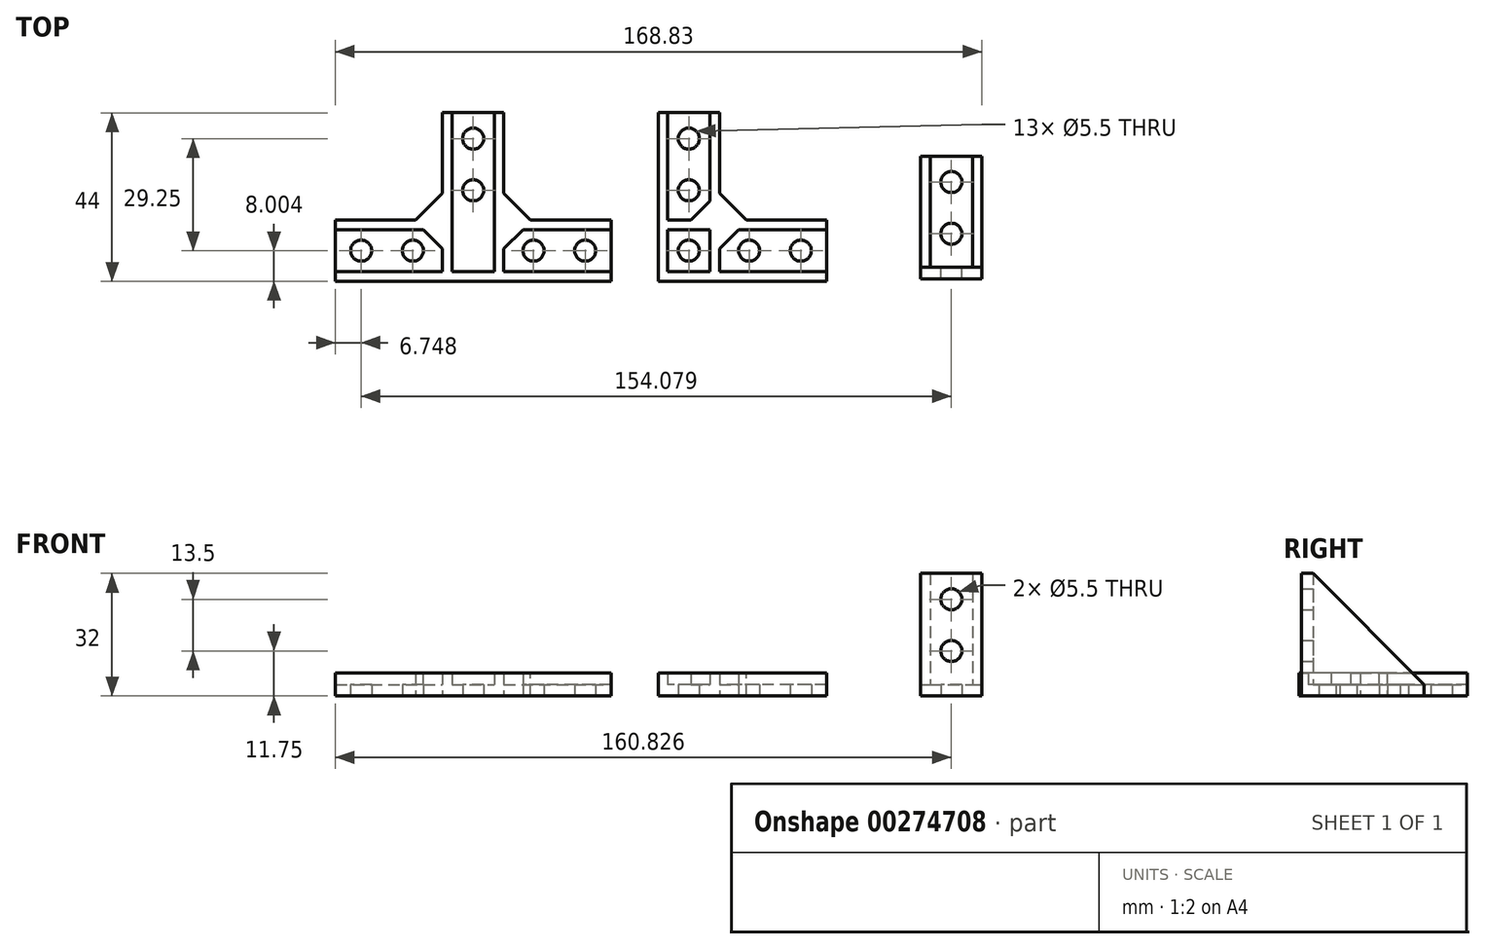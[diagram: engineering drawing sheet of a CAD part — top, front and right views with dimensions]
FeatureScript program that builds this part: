
annotation { "Feature Type Name" : "Feature", "Feature Type Description" : "" }
export const myFeature = defineFeature(function(context is Context, id is Id, definition is map)
    precondition{}
    {
        {
            var Q0;
            Q0=qCreatedBy(makeId("Top.planeOp"),FACE);
            var sketch = newSketch(context, id + "F0", { "sketchPlane" : qUnion([Q0])});
            skLineSegment(sketch, "E0", {"start": v(-54.8, -45.23) * mm, "end": v(-10.8, -45.23) * mm});
            skLineSegment(sketch, "E1", {"start": v(-10.8, -45.23) * mm, "end": v(-10.8, -29.23) * mm});
            skLineSegment(sketch, "E2", {"start": v(-10.8, -29.23) * mm, "end": v(-38.8, -29.23) * mm});
            skLineSegment(sketch, "E3", {"start": v(-38.8, -29.23) * mm, "end": v(-38.8, -1.23) * mm});
            skLineSegment(sketch, "E4", {"start": v(-38.8, -1.23) * mm, "end": v(-54.8, -1.23) * mm});
            skLineSegment(sketch, "E5", {"start": v(-54.8, -1.23) * mm, "end": v(-54.8, -45.23) * mm});
            skCircle(sketch, "E6", {"center": v(-17.54, -37.23) * mm, "radius": 2.75 * mm});
            skPoint(sketch, "E6.centerSnap0", {"position": v(-10.8, -37.23) * mm});
            skCircle(sketch, "E7", {"center": v(-31.04, -37.23) * mm, "radius": 2.75 * mm});
            skLineSegment(sketch, "E8", {"start": v(-54.8, -45.23) * mm, "end": v(-38.8, -29.23) * mm, "construction": true});
            skCircle(sketch, "E9.MirrorC", {"center": v(-46.8, -21.48) * mm, "radius": 2.75 * mm});
            skCircle(sketch, "E10.MirrorC", {"center": v(-46.8, -7.98) * mm, "radius": 2.75 * mm});
            skCircle(sketch, "E11", {"center": v(-46.8, -37.23) * mm, "radius": 2.75 * mm});
            skLineSegment(sketch, "E12", {"start": v(-67.07, -45.23) * mm, "end": v(-139.07, -45.23) * mm});
            skLineSegment(sketch, "E13", {"start": v(-139.07, -45.23) * mm, "end": v(-139.07, -29.23) * mm});
            skLineSegment(sketch, "E14", {"start": v(-139.07, -29.23) * mm, "end": v(-111.07, -29.23) * mm});
            skLineSegment(sketch, "E15", {"start": v(-111.07, -29.23) * mm, "end": v(-111.07, -1.23) * mm});
            skLineSegment(sketch, "E16", {"start": v(-111.07, -1.23) * mm, "end": v(-95.07, -1.23) * mm});
            skLineSegment(sketch, "E17", {"start": v(-95.07, -1.23) * mm, "end": v(-95.07, -29.23) * mm});
            skLineSegment(sketch, "E18", {"start": v(-95.07, -29.23) * mm, "end": v(-67.07, -29.23) * mm});
            skLineSegment(sketch, "E19", {"start": v(-67.07, -29.23) * mm, "end": v(-67.07, -45.23) * mm});
            skCircle(sketch, "E20", {"center": v(-73.82, -37.23) * mm, "radius": 2.75 * mm});
            skPoint(sketch, "E20.centerSnap0", {"position": v(-67.07, -37.23) * mm});
            skCircle(sketch, "E21", {"center": v(-87.32, -37.23) * mm, "radius": 2.75 * mm});
            skCircle(sketch, "E22", {"center": v(-103.07, -7.98) * mm, "radius": 2.75 * mm});
            skPoint(sketch, "E22.centerSnap0", {"position": v(-103.07, -1.23) * mm});
            skCircle(sketch, "E23", {"center": v(-103.07, -21.48) * mm, "radius": 2.75 * mm});
            skLineSegment(sketch, "E24", {"start": v(-103.07, -1.23) * mm, "end": v(-103.07, -45.23) * mm, "construction": true});
            skCircle(sketch, "E25.MirrorC", {"center": v(-118.82, -37.23) * mm, "radius": 2.75 * mm});
            skCircle(sketch, "E26.MirrorC", {"center": v(-132.32, -37.23) * mm, "radius": 2.75 * mm});
            skLineSegment(sketch, "E27", {"start": v(13.76, -44.56) * mm, "end": v(13.76, -12.56) * mm});
            skLineSegment(sketch, "E28", {"start": v(13.76, -12.56) * mm, "end": v(29.76, -12.56) * mm});
            skLineSegment(sketch, "E29", {"start": v(29.76, -12.56) * mm, "end": v(29.76, -44.56) * mm});
            skLineSegment(sketch, "E30", {"start": v(29.76, -44.56) * mm, "end": v(13.76, -44.56) * mm});
            skLineSegment(sketch, "E31", {"start": v(21.76, -12.56) * mm, "end": v(21.76, -44.56) * mm, "construction": true});
            skCircle(sketch, "E32", {"center": v(21.76, -19.3) * mm, "radius": 2.75 * mm});
            skCircle(sketch, "E33", {"center": v(21.76, -32.8) * mm, "radius": 2.75 * mm});
            skSolve(sketch);
        }
        {
            var Q0;
            Q0=qSketchRegion(id+"F0",true);
            extrude(context, id + "F1", {"entities" : qUnion([Q0]), "depth" : 3 * mm});
        }
        {
            var Q0;
            Q0=makeQuery(id+"F1.opExtrude","CAP_FACE",FACE,{"disambiguationData":[OSD([sQuery(id+"F0.wireOp",EDGE,"E0"),sQuery(id+"F0.wireOp",EDGE,"E1"),sQuery(id+"F0.wireOp",EDGE,"E2"),sQuery(id+"F0.wireOp",EDGE,"E3"),sQuery(id+"F0.wireOp",EDGE,"E4"),sQuery(id+"F0.wireOp",EDGE,"E5"),sQuery(id+"F0.wireOp",EDGE,"E6"),sQuery(id+"F0.wireOp",EDGE,"E7"),sQuery(id+"F0.wireOp",EDGE,"E9.MirrorC"),sQuery(id+"F0.wireOp",EDGE,"E10.MirrorC"),sQuery(id+"F0.wireOp",EDGE,"E11")])],"isStart":false});
            var sketch = newSketch(context, id + "F2", { "sketchPlane" : qUnion([Q0])});
            skLineSegment(sketch, "E34", {"start": v(-10.8, -45.23) * mm, "end": v(-10.8, -42.73) * mm});
            skLineSegment(sketch, "E35", {"start": v(-10.8, -42.73) * mm, "end": v(-52.3, -42.73) * mm});
            skLineSegment(sketch, "E36", {"start": v(-52.3, -42.73) * mm, "end": v(-52.3, -1.23) * mm});
            skLineSegment(sketch, "E37", {"start": v(-52.3, -1.23) * mm, "end": v(-54.8, -1.23) * mm});
            skLineSegment(sketch, "E38", {"start": v(-54.8, -1.23) * mm, "end": v(-54.8, -45.23) * mm});
            skLineSegment(sketch, "E39", {"start": v(-54.8, -45.23) * mm, "end": v(-10.8, -45.23) * mm});
            skLineSegment(sketch, "E40", {"start": v(-10.8, -29.23) * mm, "end": v(-10.8, -31.73) * mm});
            skLineSegment(sketch, "E41", {"start": v(-10.8, -31.73) * mm, "end": v(-41.3, -31.73) * mm});
            skLineSegment(sketch, "E42", {"start": v(-41.3, -31.73) * mm, "end": v(-41.3, -1.23) * mm});
            skLineSegment(sketch, "E43", {"start": v(-41.3, -1.23) * mm, "end": v(-38.8, -1.23) * mm});
            skLineSegment(sketch, "E44", {"start": v(-38.8, -1.23) * mm, "end": v(-38.8, -29.23) * mm});
            skLineSegment(sketch, "E45", {"start": v(-38.8, -29.23) * mm, "end": v(-10.8, -29.23) * mm});
            skLineSegment(sketch, "E46", {"start": v(-41.3, -31.73) * mm, "end": v(-41.3, -42.73) * mm});
            skLineSegment(sketch, "E47", {"start": v(-41.3, -31.73) * mm, "end": v(-52.3, -31.73) * mm});
            skLineSegment(sketch, "E48", {"start": v(-41.3, -29.23) * mm, "end": v(-52.3, -29.23) * mm});
            skLineSegment(sketch, "E49", {"start": v(-38.8, -31.73) * mm, "end": v(-38.8, -42.73) * mm});
            skLineSegment(sketch, "E50.0", {"start": v(-139.07, -29.23) * mm, "end": v(-111.07, -29.23) * mm});
            skLineSegment(sketch, "E50.1", {"start": v(-95.07, -1.23) * mm, "end": v(-95.07, -29.23) * mm});
            skLineSegment(sketch, "E50.2", {"start": v(-67.07, -45.23) * mm, "end": v(-139.07, -45.23) * mm});
            skLineSegment(sketch, "E50.3", {"start": v(-111.07, -29.23) * mm, "end": v(-111.07, -1.23) * mm});
            skLineSegment(sketch, "E50.4", {"start": v(-95.07, -29.23) * mm, "end": v(-67.07, -29.23) * mm});
            skLineSegment(sketch, "E51", {"start": v(-139.07, -45.23) * mm, "end": v(-139.07, -42.73) * mm});
            skLineSegment(sketch, "E52", {"start": v(-139.07, -42.73) * mm, "end": v(-67.07, -42.73) * mm});
            skLineSegment(sketch, "E53", {"start": v(-67.07, -45.23) * mm, "end": v(-67.07, -42.73) * mm});
            skLineSegment(sketch, "E54", {"start": v(-67.07, -29.23) * mm, "end": v(-67.07, -31.73) * mm});
            skLineSegment(sketch, "E55", {"start": v(-67.07, -31.73) * mm, "end": v(-95.07, -31.73) * mm});
            skLineSegment(sketch, "E56", {"start": v(-95.07, -31.73) * mm, "end": v(-95.07, -42.73) * mm});
            skLineSegment(sketch, "E57", {"start": v(-95.07, -1.23) * mm, "end": v(-97.57, -1.23) * mm});
            skLineSegment(sketch, "E58", {"start": v(-97.57, -1.23) * mm, "end": v(-97.57, -42.73) * mm});
            skLineSegment(sketch, "E59", {"start": v(-111.07, -1.23) * mm, "end": v(-108.57, -1.23) * mm});
            skLineSegment(sketch, "E60", {"start": v(-108.57, -1.23) * mm, "end": v(-108.57, -42.73) * mm});
            skLineSegment(sketch, "E61", {"start": v(-139.07, -29.23) * mm, "end": v(-139.07, -31.73) * mm});
            skLineSegment(sketch, "E62", {"start": v(-139.07, -31.73) * mm, "end": v(-111.07, -31.73) * mm});
            skLineSegment(sketch, "E63", {"start": v(-111.07, -31.73) * mm, "end": v(-111.07, -42.73) * mm});
            skSolve(sketch);
        }
        {
            var Q0;
            Q0=qSketchRegion(id+"F2",true);
            extrude(context, id + "F3", {"entities" : qUnion([Q0]), "operationType" : NewBodyOperationType.ADD, "depth" : 3 * mm});
        }
        {
            var Q0;
            Q0=makeQuery(id+"F3.boolean.opBoolean","MERGE",EDGE,{"derivedFrom":[makeQuery(id+"F1.opExtrude","SWEPT_EDGE",EDGE,{"disambiguationData":[OSD([sQuery(id+"F0.wireOp",EDGE,"E17"),sQuery(id+"F0.wireOp",EDGE,"E18")])]}),makeQuery(id+"F3.opExtrude","SWEPT_EDGE",EDGE,{"disambiguationData":[OSD([sQuery(id+"F2.wireOp",EDGE,"E50.1"),sQuery(id+"F2.wireOp",EDGE,"E50.4")])]})]});
            var Q1;
            Q1=makeQuery(id+"F3.boolean.opBoolean","MERGE",EDGE,{"derivedFrom":[makeQuery(id+"F1.opExtrude","SWEPT_EDGE",EDGE,{"disambiguationData":[OSD([sQuery(id+"F0.wireOp",EDGE,"E2"),sQuery(id+"F0.wireOp",EDGE,"E3")])]}),makeQuery(id+"F3.opExtrude","SWEPT_EDGE",EDGE,{"disambiguationData":[OSD([sQuery(id+"F2.wireOp",EDGE,"E44"),sQuery(id+"F2.wireOp",EDGE,"E45")])]})]});
            var Q2;
            Q2=makeQuery(id+"F3.boolean.opBoolean","MERGE",EDGE,{"derivedFrom":[makeQuery(id+"F1.opExtrude","SWEPT_EDGE",EDGE,{"disambiguationData":[OSD([sQuery(id+"F0.wireOp",EDGE,"E14"),sQuery(id+"F0.wireOp",EDGE,"E15")])]}),makeQuery(id+"F3.opExtrude","SWEPT_EDGE",EDGE,{"disambiguationData":[OSD([sQuery(id+"F2.wireOp",EDGE,"E50.0"),sQuery(id+"F2.wireOp",EDGE,"E50.3")])]})]});
            chamfer(context, id + "F4", {"entities" : qUnion([Q0, Q1, Q2]), "width" : 7 * mm, "tangentPropagation" : true});
        }
        {
            var Q0;
            Q0=makeQuery(id+"F3.opExtrude","SWEPT_EDGE",EDGE,{"disambiguationData":[OSD([sQuery(id+"F2.wireOp",EDGE,"E55"),sQuery(id+"F2.wireOp",EDGE,"E56")])]});
            var Q1;
            Q1=makeQuery(id+"F3.opExtrude","SWEPT_EDGE",EDGE,{"disambiguationData":[OSD([sQuery(id+"F2.wireOp",EDGE,"E41"),sQuery(id+"F2.wireOp",EDGE,"E49")])]});
            var Q2;
            Q2=makeQuery(id+"F3.opExtrude","SWEPT_EDGE",EDGE,{"disambiguationData":[OSD([sQuery(id+"F2.wireOp",EDGE,"E62"),sQuery(id+"F2.wireOp",EDGE,"E63")])]});
            var Q3;
            Q3=makeQuery(id+"F3.opExtrude","SWEPT_EDGE",EDGE,{"disambiguationData":[OSD([sQuery(id+"F2.wireOp",EDGE,"E42"),sQuery(id+"F2.wireOp",EDGE,"E48")])]});
            chamfer(context, id + "F5", {"entities" : qUnion([Q0, Q1, Q2, Q3]), "width" : 5 * mm, "tangentPropagation" : true});
        }
        {
            var Q0;
            Q0=makeQuery(id+"F1.opExtrude","CAP_FACE",FACE,{"disambiguationData":[OSD([sQuery(id+"F0.wireOp",EDGE,"E27"),sQuery(id+"F0.wireOp",EDGE,"E28"),sQuery(id+"F0.wireOp",EDGE,"E29"),sQuery(id+"F0.wireOp",EDGE,"E30"),sQuery(id+"F0.wireOp",EDGE,"E32"),sQuery(id+"F0.wireOp",EDGE,"E33")])],"isStart":false});
            var sketch = newSketch(context, id + "F6", { "sketchPlane" : qUnion([Q0])});
            skLineSegment(sketch, "E64.bottom", {"start": v(13.76, -44.56) * mm, "end": v(29.76, -44.56) * mm});
            skLineSegment(sketch, "E64.top", {"start": v(13.76, -41.56) * mm, "end": v(29.76, -41.56) * mm});
            skLineSegment(sketch, "E64.left", {"start": v(13.76, -44.56) * mm, "end": v(13.76, -41.56) * mm});
            skLineSegment(sketch, "E64.right", {"start": v(29.76, -44.56) * mm, "end": v(29.76, -41.56) * mm});
            skSolve(sketch);
        }
        {
            var Q0;
            Q0=qSketchRegion(id+"F6",true);
            extrude(context, id + "F7", {"entities" : qUnion([Q0]), "operationType" : NewBodyOperationType.ADD, "depth" : 29 * mm});
        }
        {
            var Q0;
            Q0=makeQuery(id+"F7.opExtrude","SWEPT_FACE",FACE,{"disambiguationData":[OSD([sQuery(id+"F6.wireOp",EDGE,"E64.top")])]});
            var sketch = newSketch(context, id + "F8", { "sketchPlane" : qUnion([Q0])});
            skCircle(sketch, "E65", {"center": v(-21.76, 25.25) * mm, "radius": 2.75 * mm});
            skCircle(sketch, "E66", {"center": v(-21.76, 11.75) * mm, "radius": 2.75 * mm});
            skLineSegment(sketch, "E67.0", {"start": v(-13.76, 32) * mm, "end": v(-29.76, 32) * mm, "construction": true});
            skLineSegment(sketch, "E68", {"start": v(-21.76, 32) * mm, "end": v(-21.76, 3) * mm, "construction": true});
            skSolve(sketch);
        }
        {
            var Q0;
            Q0=qSketchRegion(id+"F8",true);
            extrude(context, id + "F9", {"entities" : qUnion([Q0]), "operationType" : NewBodyOperationType.REMOVE, "oppositeDirection" : true, "depth" : 25 * mm});
        }
        {
            var Q0;
            Q0=makeQuery(id+"F7.boolean.opBoolean","MERGE",FACE,{"derivedFrom":[makeQuery(id+"F1.opExtrude","SWEPT_FACE",FACE,{"disambiguationData":[OSD([sQuery(id+"F0.wireOp",EDGE,"E29")])]}),makeQuery(id+"F7.opExtrude","SWEPT_FACE",FACE,{"disambiguationData":[OSD([sQuery(id+"F6.wireOp",EDGE,"E64.right")])]})]});
            var sketch = newSketch(context, id + "F10", { "sketchPlane" : qUnion([Q0])});
            skLineSegment(sketch, "E69.0", {"start": v(-41.56, 32) * mm, "end": v(-41.56, 3) * mm});
            skLineSegment(sketch, "E69.1", {"start": v(-12.56, 3) * mm, "end": v(-41.56, 3) * mm});
            skLineSegment(sketch, "E70", {"start": v(-41.56, 32) * mm, "end": v(-12.56, 3) * mm});
            skSolve(sketch);
        }
        {
            var Q0;
            Q0=qSketchRegion(id+"F10",true);
            extrude(context, id + "F11", {"entities" : qUnion([Q0]), "operationType" : NewBodyOperationType.ADD, "oppositeDirection" : true, "depth" : 2.5 * mm});
        }
        {
            var Q0;
            Q0=makeQuery(id+"F7.boolean.opBoolean","MERGE",FACE,{"derivedFrom":[makeQuery(id+"F1.opExtrude","SWEPT_FACE",FACE,{"disambiguationData":[OSD([sQuery(id+"F0.wireOp",EDGE,"E27")])]}),makeQuery(id+"F7.opExtrude","SWEPT_FACE",FACE,{"disambiguationData":[OSD([sQuery(id+"F6.wireOp",EDGE,"E64.left")])]})]});
            var sketch = newSketch(context, id + "F12", { "sketchPlane" : qUnion([Q0])});
            skLineSegment(sketch, "E71.0", {"start": v(41.56, 3) * mm, "end": v(12.56, 3) * mm});
            skLineSegment(sketch, "E71.1", {"start": v(41.56, 32) * mm, "end": v(41.56, 3) * mm});
            skLineSegment(sketch, "E72", {"start": v(41.56, 32) * mm, "end": v(12.56, 3) * mm});
            skSolve(sketch);
        }
        {
            var Q0;
            Q0=qSketchRegion(id+"F12",true);
            extrude(context, id + "F13", {"entities" : qUnion([Q0]), "operationType" : NewBodyOperationType.ADD, "oppositeDirection" : true, "depth" : 2.5 * mm});
        }
    });
